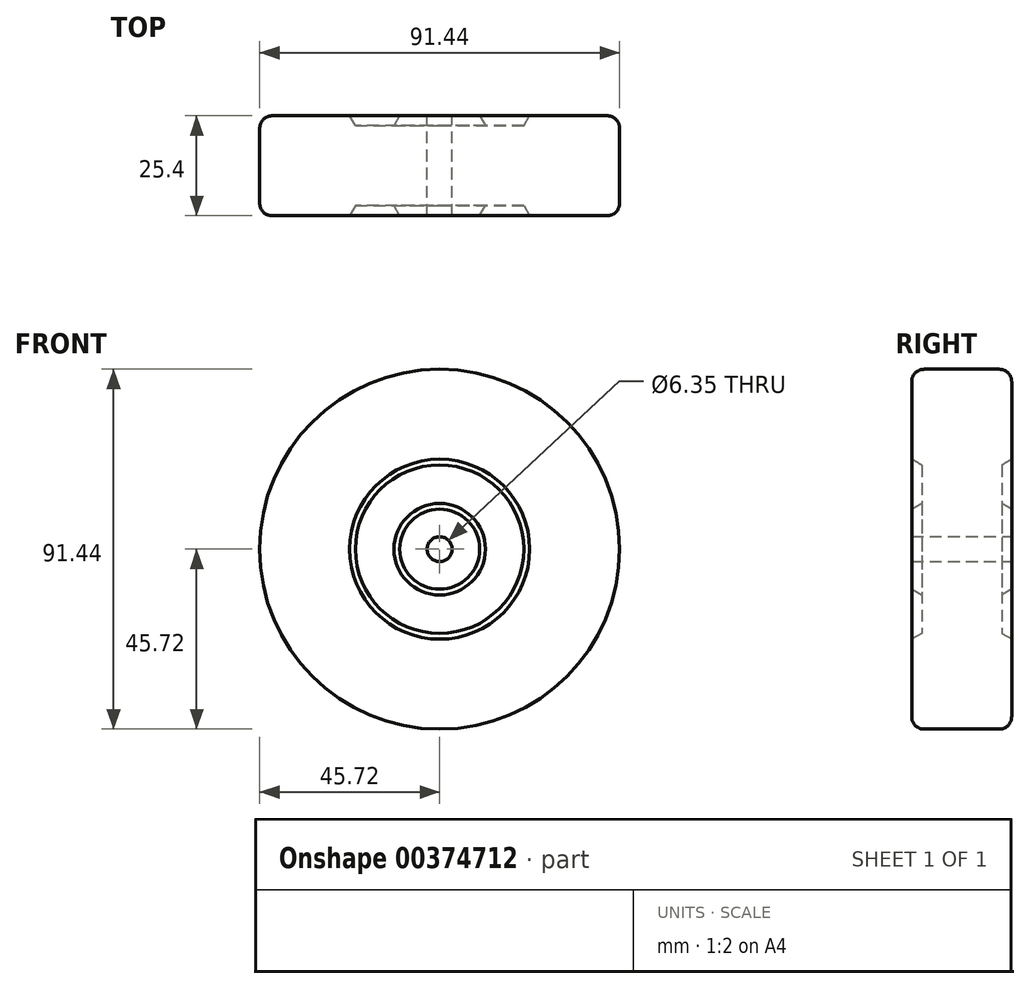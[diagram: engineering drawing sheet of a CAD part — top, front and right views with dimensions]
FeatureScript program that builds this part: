
annotation { "Feature Type Name" : "Feature", "Feature Type Description" : "" }
export const myFeature = defineFeature(function(context is Context, id is Id, definition is map)
    precondition{}
    {
        {
            var Q0;
            Q0=qCreatedBy(makeId("Right.planeOp"),FACE);
            var sketch = newSketch(context, id + "F0", { "sketchPlane" : qUnion([Q0])});
            skLineSegment(sketch, "E0", {"start": v(0, 0) * mm, "end": v(45.88, 0) * mm, "construction": true});
            skLineSegment(sketch, "E1", {"start": v(12.7, 3.18) * mm, "end": v(12.7, 10.16) * mm});
            skLineSegment(sketch, "E2", {"start": v(12.7, 10.16) * mm, "end": v(10.16, 11.63) * mm});
            skLineSegment(sketch, "E3", {"start": v(10.16, 11.63) * mm, "end": v(10.16, 21.4) * mm});
            skLineSegment(sketch, "E4", {"start": v(10.16, 21.4) * mm, "end": v(12.7, 22.86) * mm});
            skLineSegment(sketch, "E5", {"start": v(12.7, 22.86) * mm, "end": v(12.7, 42.55) * mm});
            skLineSegment(sketch, "E6.MirrorCS", {"start": v(-10.16, 21.4) * mm, "end": v(-12.7, 22.86) * mm});
            skLineSegment(sketch, "E7.MirrorCS", {"start": v(-12.7, 10.16) * mm, "end": v(-10.16, 11.63) * mm});
            skLineSegment(sketch, "E8.MirrorCS", {"start": v(-10.16, 11.63) * mm, "end": v(-10.16, 21.4) * mm});
            skLineSegment(sketch, "E9.MirrorCS", {"start": v(0, 0) * mm, "end": v(-45.88, 0) * mm, "construction": true});
            skLineSegment(sketch, "E10.MirrorCS", {"start": v(-12.7, 3.18) * mm, "end": v(-12.7, 10.16) * mm});
            skLineSegment(sketch, "E11.MirrorCS", {"start": v(-12.7, 22.86) * mm, "end": v(-12.7, 42.55) * mm});
            skLineSegment(sketch, "E12", {"start": v(-9.52, 45.72) * mm, "end": v(9.52, 45.72) * mm});
            skPoint(sketch, "E13.visualSharp", {"position": v(-12.7, 45.72) * mm});
            skArc(sketch, "E13.filletArc", {"start": v(-9.52, 45.72) * mm, "mid": v(-11.77, 44.8) * mm, "end": v(-12.7, 42.55) * mm});
            skPoint(sketch, "E14.visualSharp", {"position": v(12.7, 45.72) * mm});
            skArc(sketch, "E14.filletArc", {"start": v(12.7, 42.55) * mm, "mid": v(11.77, 44.8) * mm, "end": v(9.52, 45.72) * mm});
            skLineSegment(sketch, "E15", {"start": v(-12.7, 3.18) * mm, "end": v(12.7, 3.18) * mm});
            skSolve(sketch);
        }
        {
            var Q0;
            Q0=makeQuery(id+"F0.imprint","IMPRINT",FACE,{"disambiguationData":[TD([[makeQuery(id+"F0.imprint","IMPRINT",EDGE,{"derivedFrom":sQuery(id+"F0.wireOp",EDGE,"E1")}),1.0]])]});
            var Q1;
            Q1=sQuery(id+"F0.wireOp",EDGE,"E9.MirrorCS");
            revolve(context, id + "F1", {"entities" : qUnion([Q0]), "axis" : qUnion([Q1]), "revolveType" : RevolveType.FULL});
        }
    });
